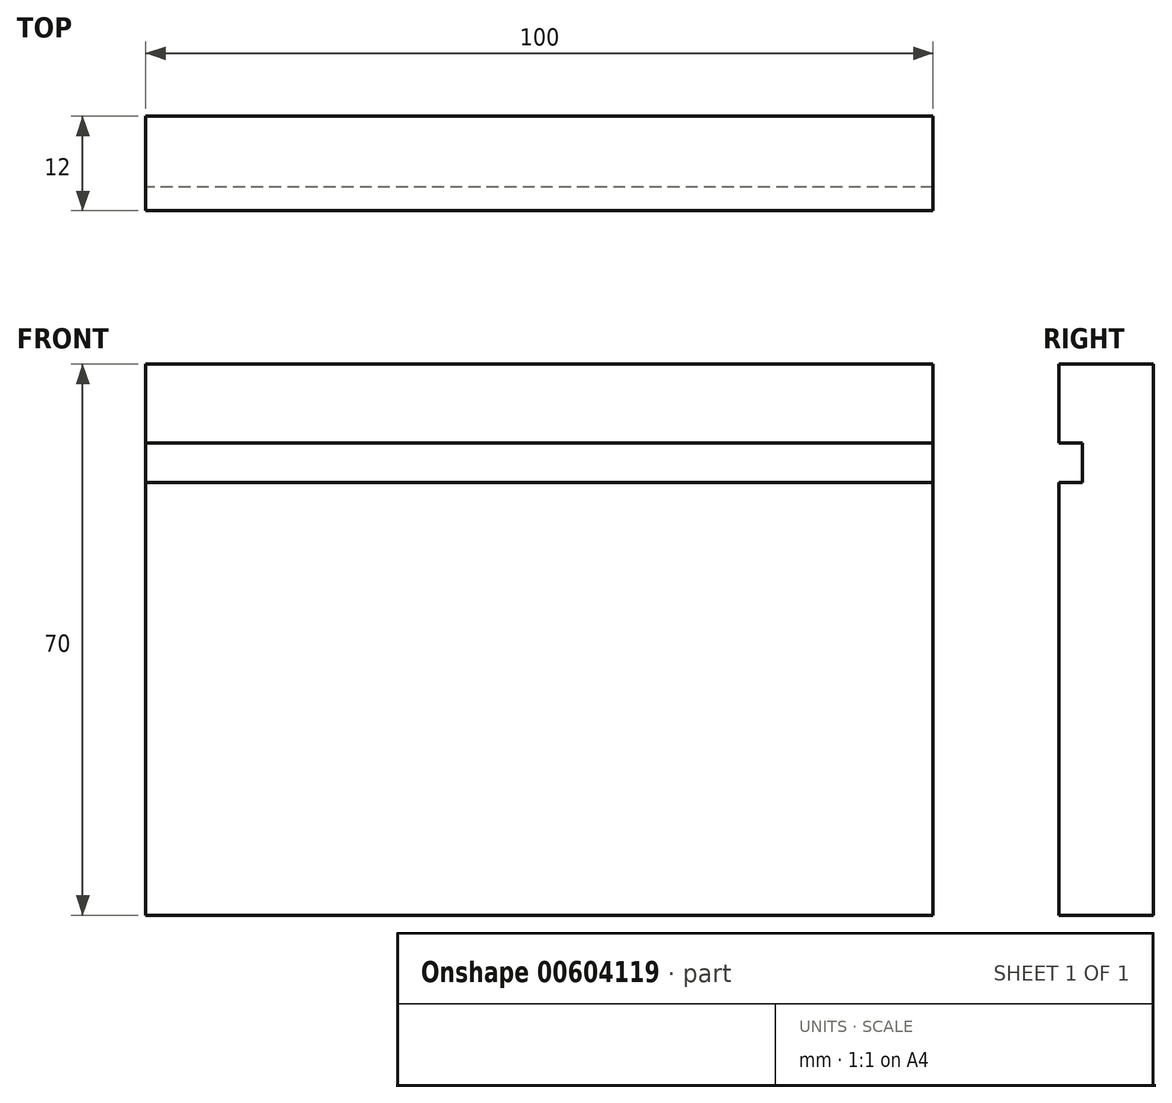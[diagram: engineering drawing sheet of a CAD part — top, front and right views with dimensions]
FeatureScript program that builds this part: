
annotation { "Feature Type Name" : "Feature", "Feature Type Description" : "" }
export const myFeature = defineFeature(function(context is Context, id is Id, definition is map)
    precondition{}
    {
        {
            var Q0;
            Q0=qCreatedBy(makeId("Right.planeOp"),FACE);
            var sketch = newSketch(context, id + "F0", { "sketchPlane" : qUnion([Q0])});
            skLineSegment(sketch, "E0", {"start": v(0, 0) * mm, "end": v(0, 70) * mm});
            skLineSegment(sketch, "E1", {"start": v(0, 70) * mm, "end": v(-12, 70) * mm});
            skLineSegment(sketch, "E2", {"start": v(-12, 70) * mm, "end": v(-12, 60) * mm});
            skLineSegment(sketch, "E3", {"start": v(-12, 60) * mm, "end": v(-9, 60) * mm});
            skLineSegment(sketch, "E4", {"start": v(-9, 60) * mm, "end": v(-9, 55) * mm});
            skLineSegment(sketch, "E5", {"start": v(-9, 55) * mm, "end": v(-12, 55) * mm});
            skLineSegment(sketch, "E6", {"start": v(-12, 55) * mm, "end": v(-12, 0) * mm});
            skLineSegment(sketch, "E7", {"start": v(-12, 0) * mm, "end": v(0, 0) * mm});
            skSolve(sketch);
        }
        {
            var Q0;
            Q0=makeQuery(id+"F0.imprint","IMPRINT",FACE,{"disambiguationData":[TD([[makeQuery(id+"F0.imprint","IMPRINT",EDGE,{"derivedFrom":sQuery(id+"F0.wireOp",EDGE,"E0")}),1.0]])]});
            extrude(context, id + "F1", {"entities" : qUnion([Q0]), "depth" : 900 * mm, "offsetDistance" : 25 * mm});
        }
        {
            var Q0;
            Q0=makeQuery(id+"F1.opExtrude","SWEPT_FACE",FACE,{"disambiguationData":[OSD([sQuery(id+"F0.wireOp",EDGE,"E6")])]});
            var sketch = newSketch(context, id + "F2", { "sketchPlane" : qUnion([Q0])});
            skLineSegment(sketch, "E8.bottom", {"start": v(900, 0) * mm, "end": v(100, 0) * mm});
            skLineSegment(sketch, "E8.top", {"start": v(900, 335.13) * mm, "end": v(100, 335.13) * mm});
            skLineSegment(sketch, "E8.left", {"start": v(900, 0) * mm, "end": v(900, 335.13) * mm});
            skLineSegment(sketch, "E8.right", {"start": v(100, 0) * mm, "end": v(100, 335.13) * mm});
            skSolve(sketch);
        }
        {
            var Q0;
            Q0 = qSketchRegion(id + "F2", true);
            extrude(context, id + "F3", {"entities" : qUnion([Q0]), "operationType" : NewBodyOperationType.REMOVE, "oppositeDirection" : true, "depth" : 25 * mm, "offsetDistance" : 25 * mm});
        }
    });
